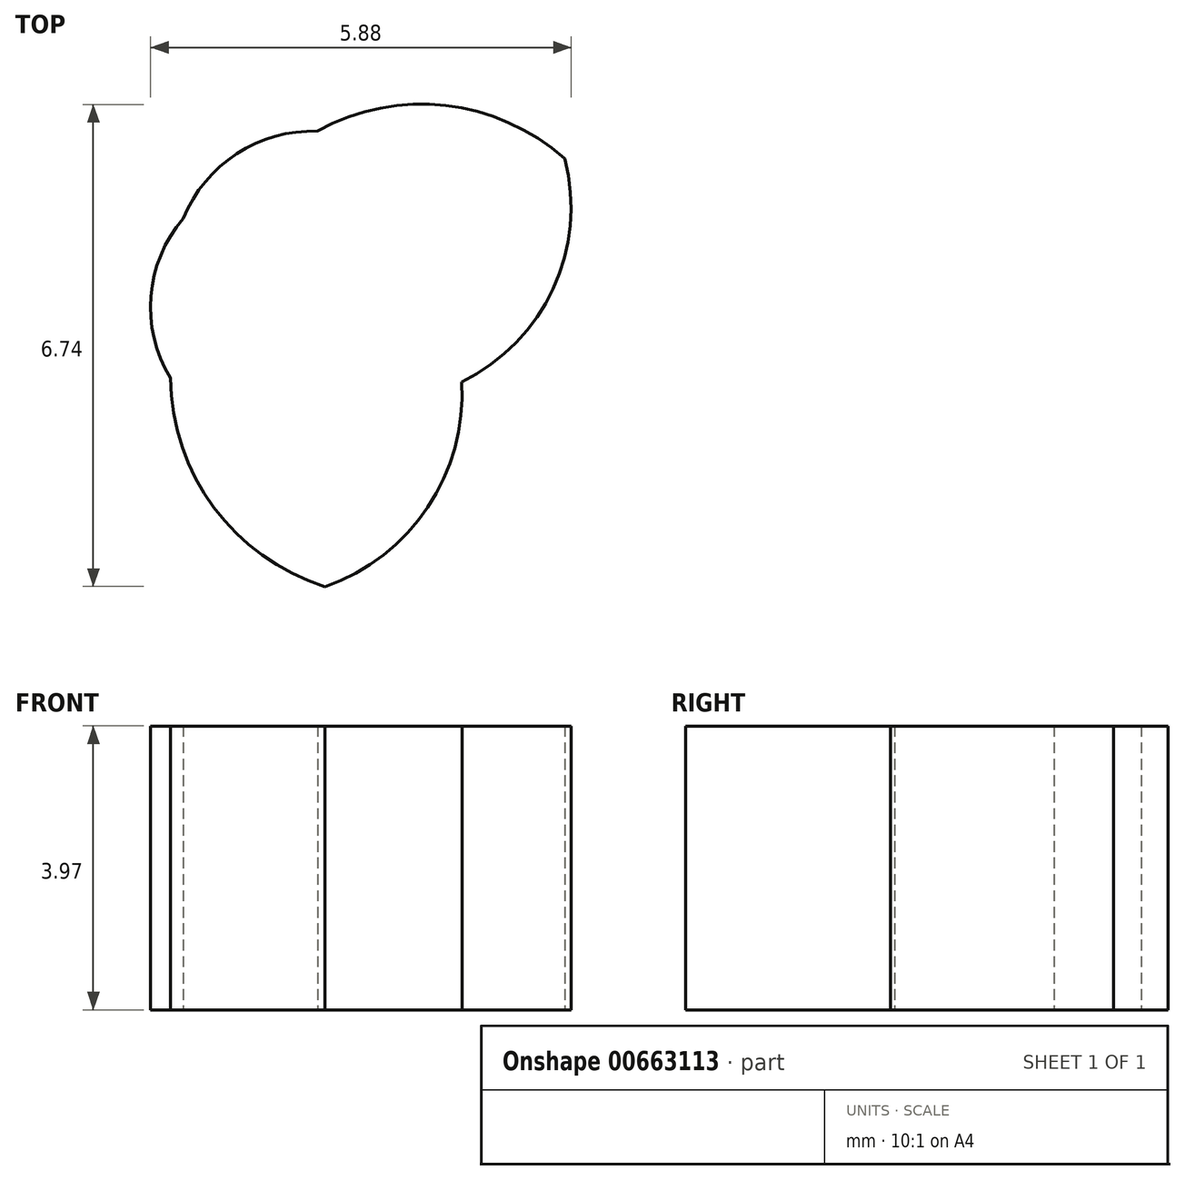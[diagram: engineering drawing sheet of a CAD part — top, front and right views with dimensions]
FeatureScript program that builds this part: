
annotation { "Feature Type Name" : "Feature", "Feature Type Description" : "" }
export const myFeature = defineFeature(function(context is Context, id is Id, definition is map)
    precondition{}
    {
        {
            var Q0;
            Q0=qCreatedBy(makeId("Top.planeOp"),FACE);
            var sketch = newSketch(context, id + "F0", { "sketchPlane" : qUnion([Q0])});
            skPoint(sketch, "E0.center", {"position": v(0, 0) * mm});
            skPoint(sketch, "E1.center", {"position": v(0.03, -0.1) * mm});
            skLineSegment(sketch, "E2", {"start": v(7.8, 0.95) * mm, "end": v(7.8, 0.95) * mm});
            skLineSegment(sketch, "E3", {"start": v(8.03, -1.52) * mm, "end": v(8.03, -1.52) * mm});
            skLineSegment(sketch, "E4", {"start": v(6.36, 3.55) * mm, "end": v(6.4, 3.5) * mm});
            skArc(sketch, "E5", {"start": v(-2.12, -1.17) * mm, "mid": v(-1.52, -2.98) * mm, "end": v(0.03, -4.1) * mm});
            skArc(sketch, "E6", {"start": v(3.39, 1.9) * mm, "mid": v(1.72, 2.64) * mm, "end": v(-0.07, 2.28) * mm});
            skArc(sketch, "E7", {"start": v(0.03, -4.1) * mm, "mid": v(1.47, -2.98) * mm, "end": v(1.95, -1.23) * mm});
            skArc(sketch, "E8", {"start": v(1.95, -1.23) * mm, "mid": v(3.23, 0.07) * mm, "end": v(3.39, 1.9) * mm});
            skArc(sketch, "E9", {"start": v(-0.07, 2.28) * mm, "mid": v(-1.2, 1.96) * mm, "end": v(-1.94, 1.06) * mm});
            skArc(sketch, "E10", {"start": v(-1.94, 1.06) * mm, "mid": v(-2.4, -0.03) * mm, "end": v(-2.12, -1.17) * mm});
            skSolve(sketch);
        }
        {
            var Q0;
            Q0=makeQuery(id+"F0.imprint","IMPRINT",FACE,{"disambiguationData":[TD([[makeQuery(id+"F0.imprint","IMPRINT",EDGE,{"derivedFrom":sQuery(id+"F0.wireOp",EDGE,"E5")}),1.0]])]});
            extrude(context, id + "F1", {"entities" : qUnion([Q0]), "depth" : 3.97 * mm, "offsetDistance" : 25.4 * mm});
        }
    });
